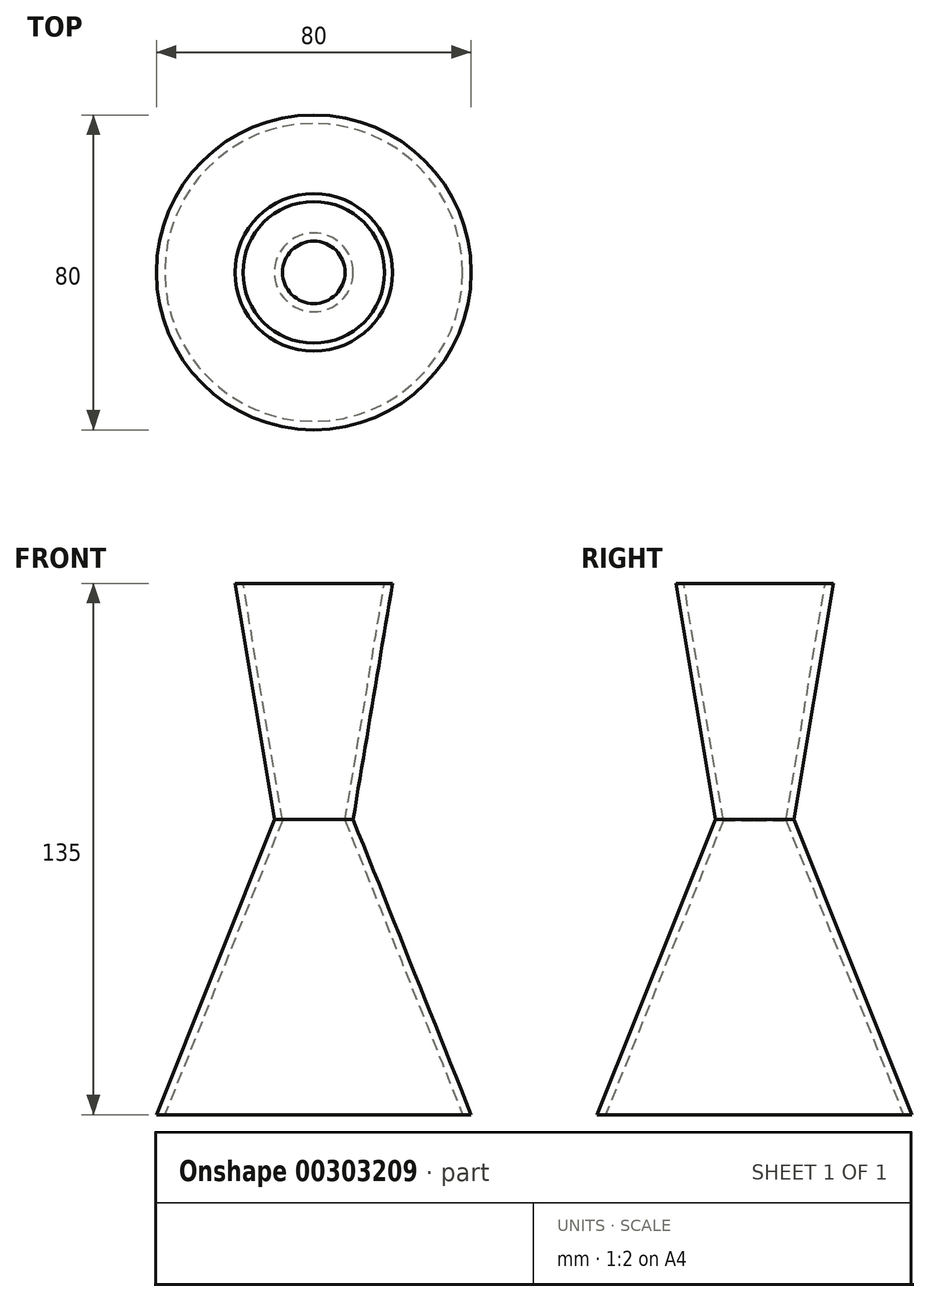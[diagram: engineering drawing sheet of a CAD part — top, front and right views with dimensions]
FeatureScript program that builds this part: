
annotation { "Feature Type Name" : "Feature", "Feature Type Description" : "" }
export const myFeature = defineFeature(function(context is Context, id is Id, definition is map)
    precondition{}
    {
        {
            var Q0;
            Q0=qCreatedBy(makeId("Front.planeOp"),FACE);
            var sketch = newSketch(context, id + "F0", { "sketchPlane" : qUnion([Q0])});
            skLineSegment(sketch, "E0.bottom", {"start": v(0, 0) * mm, "end": v(-20, 0) * mm, "construction": true});
            skLineSegment(sketch, "E0.top", {"start": v(0, 60) * mm, "end": v(-20, 60) * mm, "construction": true});
            skLineSegment(sketch, "E0.right", {"start": v(-20, 0) * mm, "end": v(-20, 60) * mm, "construction": true});
            skLineSegment(sketch, "E1.bottom", {"start": v(0, 0) * mm, "end": v(-40, 0) * mm, "construction": true});
            skLineSegment(sketch, "E1.top", {"start": v(0, -75) * mm, "end": v(-40, -75) * mm, "construction": true});
            skLineSegment(sketch, "E1.right", {"start": v(-40, 0) * mm, "end": v(-40, -75) * mm, "construction": true});
            skLineSegment(sketch, "E2", {"start": v(-20, 60) * mm, "end": v(-10, 0) * mm});
            skLineSegment(sketch, "E3", {"start": v(-10, 0) * mm, "end": v(-40, -75) * mm});
            skLineSegment(sketch, "E4", {"start": v(0, -75) * mm, "end": v(-40, -75) * mm});
            skLineSegment(sketch, "E5", {"start": v(-20, 60) * mm, "end": v(-30.16, 60) * mm});
            skLineSegment(sketch, "E6", {"start": v(-20, 60) * mm, "end": v(0, 60) * mm});
            skLineSegment(sketch, "E7", {"start": v(0, 60) * mm, "end": v(0, -75) * mm});
            skSolve(sketch);
        }
        {
            var Q0;
            Q0=makeQuery(id+"F0.imprint","IMPRINT",FACE,{"disambiguationData":[TD([[makeQuery(id+"F0.imprint","IMPRINT",EDGE,{"derivedFrom":sQuery(id+"F0.wireOp",EDGE,"E2")}),1.0]])]});
            var Q1;
            Q1=sQuery(id+"F0.wireOp",EDGE,"E7");
            revolve(context, id + "F1", {"entities" : qUnion([Q0]), "axis" : qUnion([Q1]), "revolveType" : RevolveType.FULL});
        }
        {
            var Q0;
            Q0=makeQuery(id+"F1.opRevolve","SWEPT_FACE",FACE,{"disambiguationData":[OSD([sQuery(id+"F0.wireOp",EDGE,"E4")])]});
            var Q1;
            Q1=makeQuery(id+"F1.opRevolve","SWEPT_FACE",FACE,{"disambiguationData":[OSD([sQuery(id+"F0.wireOp",EDGE,"E6")])]});
            shell(context, id + "F2", {"entities" : qUnion([Q0, Q1]), "thickness" : 2 * mm});
        }
    });
